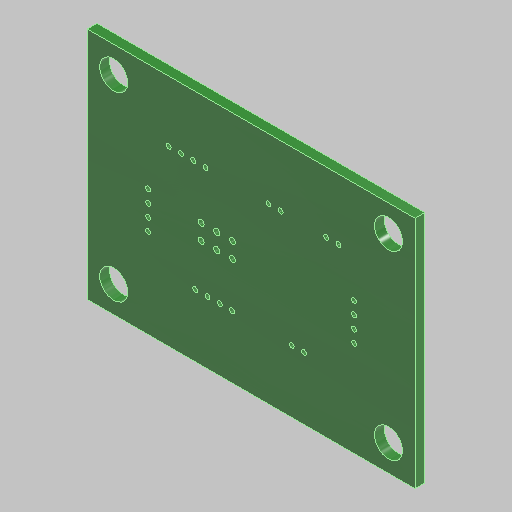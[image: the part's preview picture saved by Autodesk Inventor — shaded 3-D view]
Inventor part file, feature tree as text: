
AUTODESK INVENTOR PART (.ipt)
format: ipt  version: 2023.5 (Build 275446000, 446)  size: 185,344 bytes
history: native  units: mm
features: hole x3, extrude x1
ambient origin geometry x8: Origin, YZ Plane, XZ Plane, XY Plane, X Axis, Y Axis, Z Axis, Center Point
bodies: Solid1 (feature_tree)
feature tree (4):
  extrude  "Extrusion1"  Depth=53.34mm
  hole  "Hole1"  [1 undecoded]
  hole  "Hole2"  [1 undecoded]
  hole  "Hole3"  [1 undecoded]
note: 3 required parameter values undecoded (feature->parameter linkage not recoverable at this tier; creation-order binding heuristic only, values carry confidence <= 0.55)
